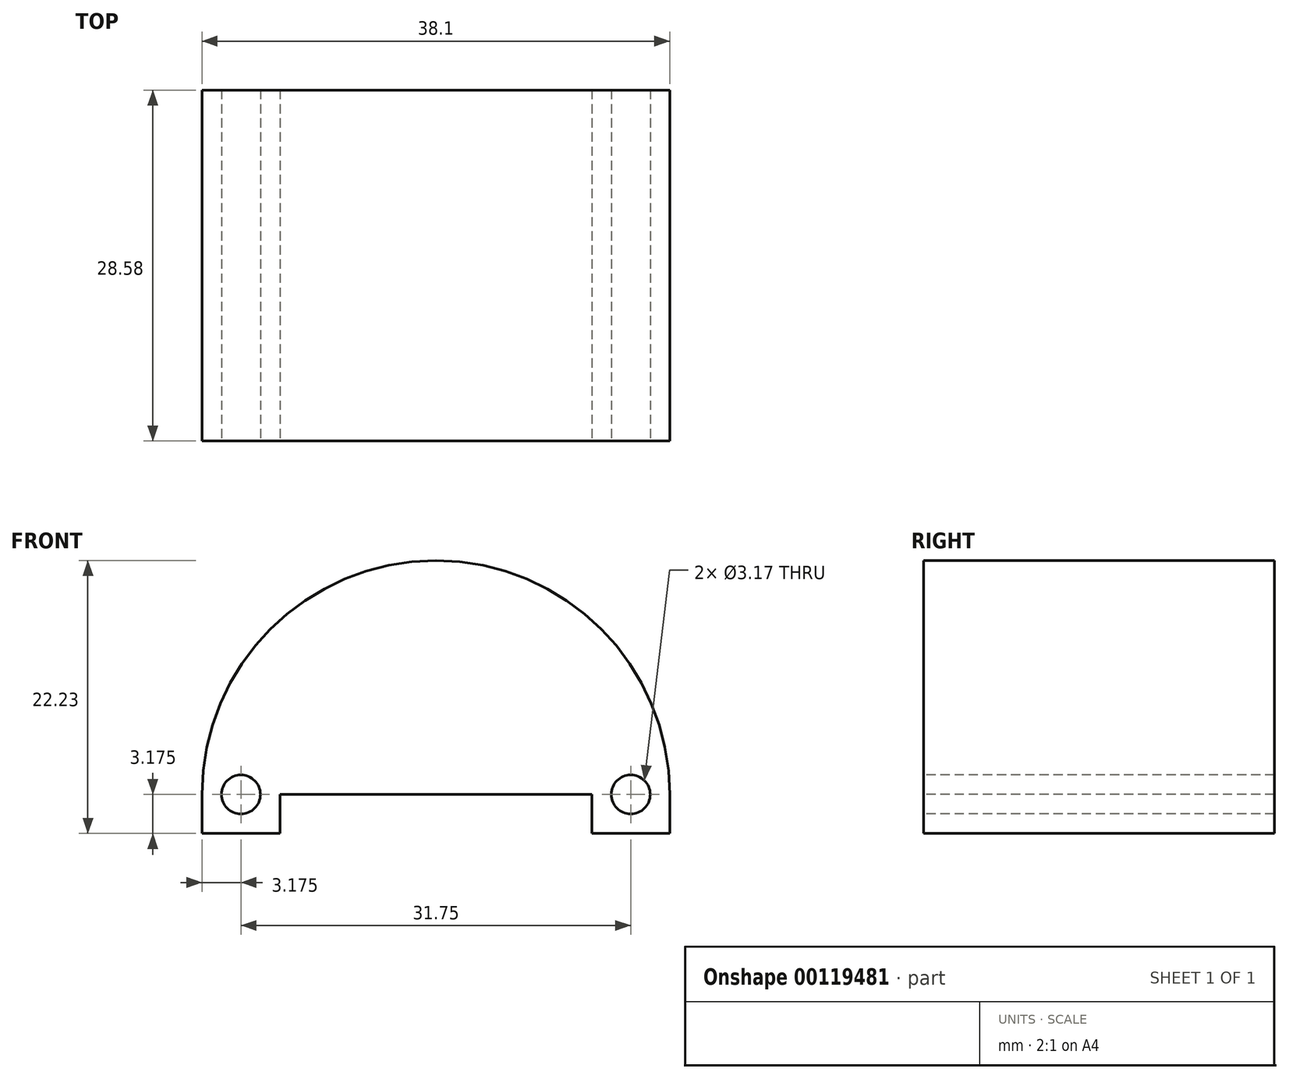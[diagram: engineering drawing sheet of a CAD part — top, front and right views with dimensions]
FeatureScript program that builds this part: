
annotation { "Feature Type Name" : "Feature", "Feature Type Description" : "" }
export const myFeature = defineFeature(function(context is Context, id is Id, definition is map)
    precondition{}
    {
        {
            var Q0;
            Q0=qCreatedBy(makeId("Top.planeOp"),FACE);
            var sketch = newSketch(context, id + "F0", { "sketchPlane" : qUnion([Q0])});
            skLineSegment(sketch, "E0.bottom", {"start": v(-12.7, 14.29) * mm, "end": v(12.7, 14.29) * mm});
            skLineSegment(sketch, "E0.top", {"start": v(-12.7, -14.29) * mm, "end": v(12.7, -14.29) * mm});
            skLineSegment(sketch, "E0.left", {"start": v(-12.7, 14.29) * mm, "end": v(-12.7, -14.29) * mm});
            skLineSegment(sketch, "E0.right", {"start": v(12.7, 14.29) * mm, "end": v(12.7, -14.29) * mm});
            skPoint(sketch, "E0.middle", {"position": v(0, 0) * mm});
            skLineSegment(sketch, "E1.bottom", {"start": v(-19.05, 14.29) * mm, "end": v(19.05, 14.29) * mm});
            skLineSegment(sketch, "E1.top", {"start": v(-19.05, -14.29) * mm, "end": v(19.05, -14.29) * mm});
            skLineSegment(sketch, "E1.left", {"start": v(-19.05, 14.29) * mm, "end": v(-19.05, -14.29) * mm});
            skLineSegment(sketch, "E1.right", {"start": v(19.05, 14.29) * mm, "end": v(19.05, -14.29) * mm});
            skSolve(sketch);
        }
        {
            var Q0;
            Q0 = qSketchRegion(id + "F0", true);
            extrude(context, id + "F1", {"entities" : qUnion([Q0]), "depth" : 22.22 * mm});
        }
        {
            var Q0;
            Q0=makeQuery(id+"F1.opExtrude","SWEPT_FACE",FACE,{"disambiguationData":[OSD([sQuery(id+"F0.wireOp",EDGE,"E1.top")])]});
            var sketch = newSketch(context, id + "F2", { "sketchPlane" : qUnion([Q0])});
            skLineSegment(sketch, "E2", {"start": v(-12.7, 0) * mm, "end": v(-12.7, 3.18) * mm});
            skLineSegment(sketch, "E3", {"start": v(-12.7, 3.18) * mm, "end": v(12.7, 3.18) * mm});
            skLineSegment(sketch, "E4", {"start": v(12.7, 3.18) * mm, "end": v(12.7, 0) * mm});
            skLineSegment(sketch, "E5", {"start": v(-12.7, 3.18) * mm, "end": v(-19.05, 3.18) * mm, "construction": true});
            skLineSegment(sketch, "E6", {"start": v(12.7, 3.18) * mm, "end": v(19.05, 3.18) * mm, "construction": true});
            skArc(sketch, "E7", {"start": v(19.05, 3.18) * mm, "mid": v(0, 22.23) * mm, "end": v(-19.05, 3.17) * mm});
            skCircle(sketch, "E8", {"center": v(-15.88, 3.18) * mm, "radius": 1.59 * mm});
            skCircle(sketch, "E9", {"center": v(15.88, 3.18) * mm, "radius": 1.59 * mm});
            skSolve(sketch);
        }
        {
            var Q0;
            {var subQ0=sQuery(id+"F2.wireOp",EDGE,"E7");var subQ1=sQuery(id+"F0.wireOp",EDGE,"E1.top");var subQ4=makeQuery(id+"F1.opExtrude","CAP_EDGE",EDGE,{"disambiguationData":[OSD([subQ1])],"isStart":false});var subQ5=makeQuery(id+"F2.imprint","INTERSECT",VERTEX,{"derivedFrom":[subQ4,subQ0]});Q0=makeQuery(id+"F2.imprint","IMPRINT",FACE,{"disambiguationData":[TD([[makeQuery(id+"F2.imprint","IMPRINT",EDGE,{"disambiguationData":[TD([[subQ5,-1.0]])],"derivedFrom":subQ0}),-1.0]])]});}
            var Q1;
            {var subQ0=sQuery(id+"F2.wireOp",EDGE,"E7");var subQ1=sQuery(id+"F0.wireOp",EDGE,"E1.top");var subQ4=makeQuery(id+"F1.opExtrude","CAP_EDGE",EDGE,{"disambiguationData":[OSD([subQ1])],"isStart":false});var subQ5=makeQuery(id+"F2.imprint","INTERSECT",VERTEX,{"derivedFrom":[subQ4,subQ0]});Q1=makeQuery(id+"F2.imprint","IMPRINT",FACE,{"disambiguationData":[TD([[makeQuery(id+"F2.imprint","IMPRINT",EDGE,{"disambiguationData":[TD([[subQ5,1.0]])],"derivedFrom":subQ0}),-1.0]])]});}
            var Q2;
            {var subQ0=sQuery(id+"F2.wireOp",EDGE,"E2");Q2=makeQuery(id+"F2.imprint","IMPRINT",FACE,{"disambiguationData":[TD([[makeQuery(id+"F2.imprint","IMPRINT",EDGE,{"derivedFrom":subQ0}),-1.0]])]});}
            var Q3;
            Q3=makeQuery(id+"F2.imprint","IMPRINT",FACE,{"disambiguationData":[TD([[makeQuery(id+"F2.imprint","IMPRINT",EDGE,{"derivedFrom":sQuery(id+"F2.wireOp",EDGE,"E8")}),1.0]])]});
            var Q4;
            Q4=makeQuery(id+"F2.imprint","IMPRINT",FACE,{"disambiguationData":[TD([[makeQuery(id+"F2.imprint","IMPRINT",EDGE,{"derivedFrom":sQuery(id+"F2.wireOp",EDGE,"E9")}),1.0]])]});
            extrude(context, id + "F3", {"entities" : qUnion([Q0, Q1, Q2, Q3, Q4]), "operationType" : NewBodyOperationType.REMOVE, "oppositeDirection" : true, "depth" : 28.57 * mm});
        }
    });
